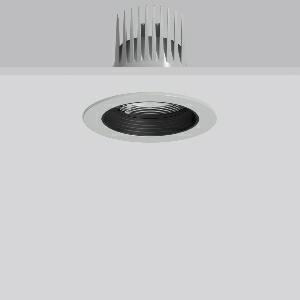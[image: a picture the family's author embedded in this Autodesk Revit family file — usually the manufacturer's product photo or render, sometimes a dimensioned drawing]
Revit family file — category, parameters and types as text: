
# Revit family: heledon_maxi_e_901768_004_1_3592
name_source: partatom
category: Lighting Fixtures
units: mm (PartAtom-declared; Revit-internal decimal feet)

## family parameters
Cut with Voids When Loaded = No
Host = Face
Light Source = No
Part Type = Normal
Room Calculation Point = No
Round Connector Dimension = Use Diameter
Shared = No

## types (1)
- HELEDON maxi E (1 x LED Modul 940, 3750 lm, 4000)
    Apparent Load = 35 VA
    Approval mark = CE
    CIE Flux Codes = 96 100 100 100 100
    Color Rendering = 92
    Color Temperature = 4000
    Default Elevation = 1800 mm
    Description = Series: HELEDON maxi
Round recessed downlight. Housing: die-cast aluminium, powder-coated. Black plastic ring and recessed LED to prevent glare from the side. Optical assembly with lens made of plastic (polycarbonate) for the best homogeneous light distribution - can be changed without tools. Best colour rendering index Ra>90. Suitable for Recessed ceiling mounting. Installation without tools thanks to spring fastening system. Including separate LED converter with connecting cable 600 mm.High quality converter without flickering and stroboscopic effect. Through-wiring box (5 pole) available as accessory. The following accessories can be mounted without use of tools: interchangeable lenses, decorative glasses, honeycomb louvre, clear and frosted diffusers, white interchangeable plastic ring. 
Colour: silver
Diameter: 162 mm
Height: 3 mm
Cut-out diameter: 152 mm
Recess height: 200 mm
Luminaire: recess height: 135 mm
Lamp: LED
Socket: without socket
Colour temperature: 4000K
Colour rendering index (CRI): 92
System power: 35 W
Rated luminous flux: 3750 lm
Luminous efficiency: 107 lm/W
Control gear: Regulated power supply
Protection class: II
Type of protection: IP 20
    Height = 0 mm  [stored 0 ft]
    Lamp = 1 x LED Modul 940
    Lamp Light Flux = 3750 lm
    Lamp count = 1
    Length = 162 mm
    Lifetime = 50000 h
    Luminous efficacy = 107 lm/W
    Manufacturer = RZB
    ModVariant = No
    Model = 901768.004.1
    Mounting Place = Ceiling
    Mounting Type = Recessed
    Number of Poles = 1
    OnlyDefault = Yes
    Power Factor = 1
    Product Name = HELEDON maxi E
    Product group = Recessed downlights
    ProductGroupID = 402
    Protection Class = Protection class II
    Protection Degree = IP 20
    RLX_Detail_Level = 1
    RLX_Emergency_Light_Flux = 0 lm
    RLX_Emergency_Type = 0
    RLX_Emergency_Type_DB = No
    RlxData = <blob elided: 118829 chars, md5=2af5420d>
    Socket = socket
    Standby Power = 0 W
    System Light Flux = 3750 lm
    System Power = 35 W
    Type Comments = Product without accessories
    Type Image = 901663.004.jpg
    URL = http://relux.com
    VarID = ---
    Voltage = 230 V
    Voltage Range = 220-240 V
    Weight = 0.00 kg
    Width = 0 mm  [stored 0 ft]

note: [stored X ft] marks values corroborated as IEEE doubles in the binary element streams (Revit-internal decimal feet)

## geometry (parser evidence)
native form markers: Blend x4, Sweep x9
no freeform markers — native parametric forms only
